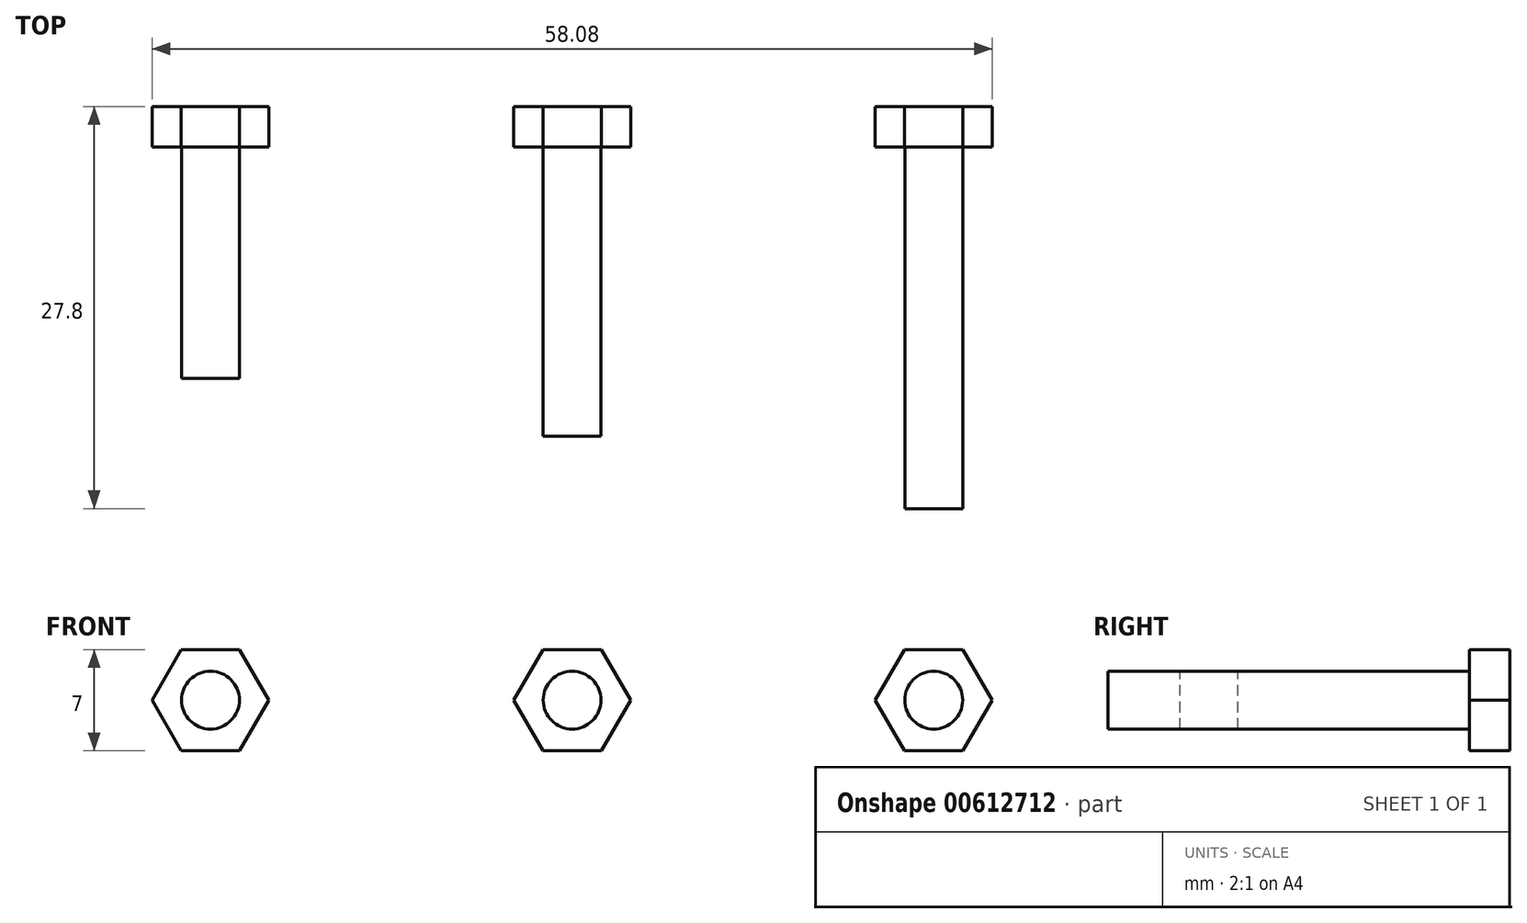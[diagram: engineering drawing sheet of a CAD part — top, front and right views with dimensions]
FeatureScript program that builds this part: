
annotation { "Feature Type Name" : "Feature", "Feature Type Description" : "" }
export const myFeature = defineFeature(function(context is Context, id is Id, definition is map)
    precondition{}
    {
        {
            var Q0;
            Q0=qCreatedBy(makeId("Front.planeOp"),FACE);
            var sketch = newSketch(context, id + "F0", { "sketchPlane" : qUnion([Q0])});
            skCircle(sketch, "E0.cCircle", {"center": v(0, 0) * mm, "radius": 3.5 * mm, "construction": true});
            skLineSegment(sketch, "E0.0", {"start": v(2.02, 3.5) * mm, "end": v(4.04, 0) * mm});
            skLineSegment(sketch, "E0.1", {"start": v(4.04, 0) * mm, "end": v(2.02, -3.5) * mm});
            skLineSegment(sketch, "E0.2", {"start": v(2.02, -3.5) * mm, "end": v(-2.02, -3.5) * mm});
            skLineSegment(sketch, "E0.3", {"start": v(-2.02, -3.5) * mm, "end": v(-4.04, 0) * mm});
            skLineSegment(sketch, "E0.4", {"start": v(-4.04, 0) * mm, "end": v(-2.02, 3.5) * mm});
            skLineSegment(sketch, "E0.5", {"start": v(-2.02, 3.5) * mm, "end": v(2.02, 3.5) * mm});
            skPoint(sketch, "E0.0.midPoint", {"position": v(3.03, 1.75) * mm});
            skLineSegment(sketch, "E1.1.0.0", {"start": v(27.02, 3.5) * mm, "end": v(29.04, 0) * mm});
            skLineSegment(sketch, "E1.1.0.1", {"start": v(29.04, 0) * mm, "end": v(27.02, -3.5) * mm});
            skLineSegment(sketch, "E1.1.0.2", {"start": v(27.02, -3.5) * mm, "end": v(22.98, -3.5) * mm});
            skLineSegment(sketch, "E1.1.0.3", {"start": v(22.98, -3.5) * mm, "end": v(20.96, 0) * mm});
            skLineSegment(sketch, "E1.1.0.4", {"start": v(20.96, 0) * mm, "end": v(22.98, 3.5) * mm});
            skLineSegment(sketch, "E1.1.0.5", {"start": v(22.98, 3.5) * mm, "end": v(27.02, 3.5) * mm});
            skPoint(sketch, "E1.1.0.6", {"position": v(28.03, 1.75) * mm});
            skCircle(sketch, "E1.1.0.7", {"center": v(25, 0) * mm, "radius": 3.5 * mm, "construction": true});
            skLineSegment(sketch, "E1.2.0.0", {"start": v(52.02, 3.5) * mm, "end": v(54.04, 0) * mm});
            skLineSegment(sketch, "E1.2.0.1", {"start": v(54.04, 0) * mm, "end": v(52.02, -3.5) * mm});
            skLineSegment(sketch, "E1.2.0.2", {"start": v(52.02, -3.5) * mm, "end": v(47.98, -3.5) * mm});
            skLineSegment(sketch, "E1.2.0.3", {"start": v(47.98, -3.5) * mm, "end": v(45.96, 0) * mm});
            skLineSegment(sketch, "E1.2.0.4", {"start": v(45.96, 0) * mm, "end": v(47.98, 3.5) * mm});
            skLineSegment(sketch, "E1.2.0.5", {"start": v(47.98, 3.5) * mm, "end": v(52.02, 3.5) * mm});
            skPoint(sketch, "E1.2.0.6", {"position": v(53.03, 1.75) * mm});
            skCircle(sketch, "E1.2.0.7", {"center": v(50, 0) * mm, "radius": 3.5 * mm, "construction": true});
            skLineSegment(sketch, "E1.direction1", {"start": v(-2.02, -3.5) * mm, "end": v(22.98, -3.5) * mm, "construction": true});
            skSolve(sketch);
        }
        {
            var Q0;
            Q0=makeQuery(id+"F0.imprint","IMPRINT",FACE,{"disambiguationData":[TD([[makeQuery(id+"F0.imprint","IMPRINT",EDGE,{"derivedFrom":sQuery(id+"F0.wireOp",EDGE,"E0.0")}),-1.0]])]});
            var Q1;
            Q1=makeQuery(id+"F0.imprint","IMPRINT",FACE,{"disambiguationData":[TD([[makeQuery(id+"F0.imprint","IMPRINT",EDGE,{"derivedFrom":sQuery(id+"F0.wireOp",EDGE,"E1.1.0.0")}),-1.0]])]});
            var Q2;
            Q2=makeQuery(id+"F0.imprint","IMPRINT",FACE,{"disambiguationData":[TD([[makeQuery(id+"F0.imprint","IMPRINT",EDGE,{"derivedFrom":sQuery(id+"F0.wireOp",EDGE,"E1.2.0.0")}),-1.0]])]});
            extrude(context, id + "F1", {"entities" : qUnion([Q0, Q1, Q2]), "depth" : 2.8 * mm, "offsetDistance" : 25 * mm});
        }
        {
            var Q0;
            Q0=makeQuery(id+"F1.opExtrude","CAP_FACE",FACE,{"disambiguationData":[OSD([sQuery(id+"F0.wireOp",EDGE,"E0.0"),sQuery(id+"F0.wireOp",EDGE,"E0.1"),sQuery(id+"F0.wireOp",EDGE,"E0.2"),sQuery(id+"F0.wireOp",EDGE,"E0.3"),sQuery(id+"F0.wireOp",EDGE,"E0.4"),sQuery(id+"F0.wireOp",EDGE,"E0.5")])],"isStart":false});
            var sketch = newSketch(context, id + "F2", { "sketchPlane" : qUnion([Q0])});
            skCircle(sketch, "E2", {"center": v(0, 0) * mm, "radius": 2 * mm});
            skCircle(sketch, "E3.1.0.0", {"center": v(25, 0) * mm, "radius": 2 * mm});
            skCircle(sketch, "E3.2.0.0", {"center": v(50, 0) * mm, "radius": 2 * mm});
            skLineSegment(sketch, "E3.direction1", {"start": v(0, 0) * mm, "end": v(25, 0) * mm, "construction": true});
            skSolve(sketch);
        }
        {
            var Q0;
            Q0=makeQuery(id+"F2.imprint","IMPRINT",FACE,{"disambiguationData":[TD([[makeQuery(id+"F2.imprint","IMPRINT",EDGE,{"derivedFrom":sQuery(id+"F2.wireOp",EDGE,"E2")}),1.0]])]});
            extrude(context, id + "F3", {"entities" : qUnion([Q0]), "operationType" : NewBodyOperationType.ADD, "depth" : 16 * mm, "offsetDistance" : 25 * mm});
        }
        {
            var Q0;
            Q0=makeQuery(id+"F2.imprint","IMPRINT",FACE,{"disambiguationData":[TD([[makeQuery(id+"F2.imprint","IMPRINT",EDGE,{"derivedFrom":sQuery(id+"F2.wireOp",EDGE,"E3.1.0.0")}),1.0]])]});
            extrude(context, id + "F4", {"entities" : qUnion([Q0]), "operationType" : NewBodyOperationType.ADD, "depth" : 20 * mm, "offsetDistance" : 25 * mm});
        }
        {
            var Q0;
            Q0=makeQuery(id+"F2.imprint","IMPRINT",FACE,{"disambiguationData":[TD([[makeQuery(id+"F2.imprint","IMPRINT",EDGE,{"derivedFrom":sQuery(id+"F2.wireOp",EDGE,"E3.2.0.0")}),1.0]])]});
            extrude(context, id + "F5", {"entities" : qUnion([Q0]), "operationType" : NewBodyOperationType.ADD, "depth" : 25 * mm, "offsetDistance" : 25 * mm});
        }
    });
